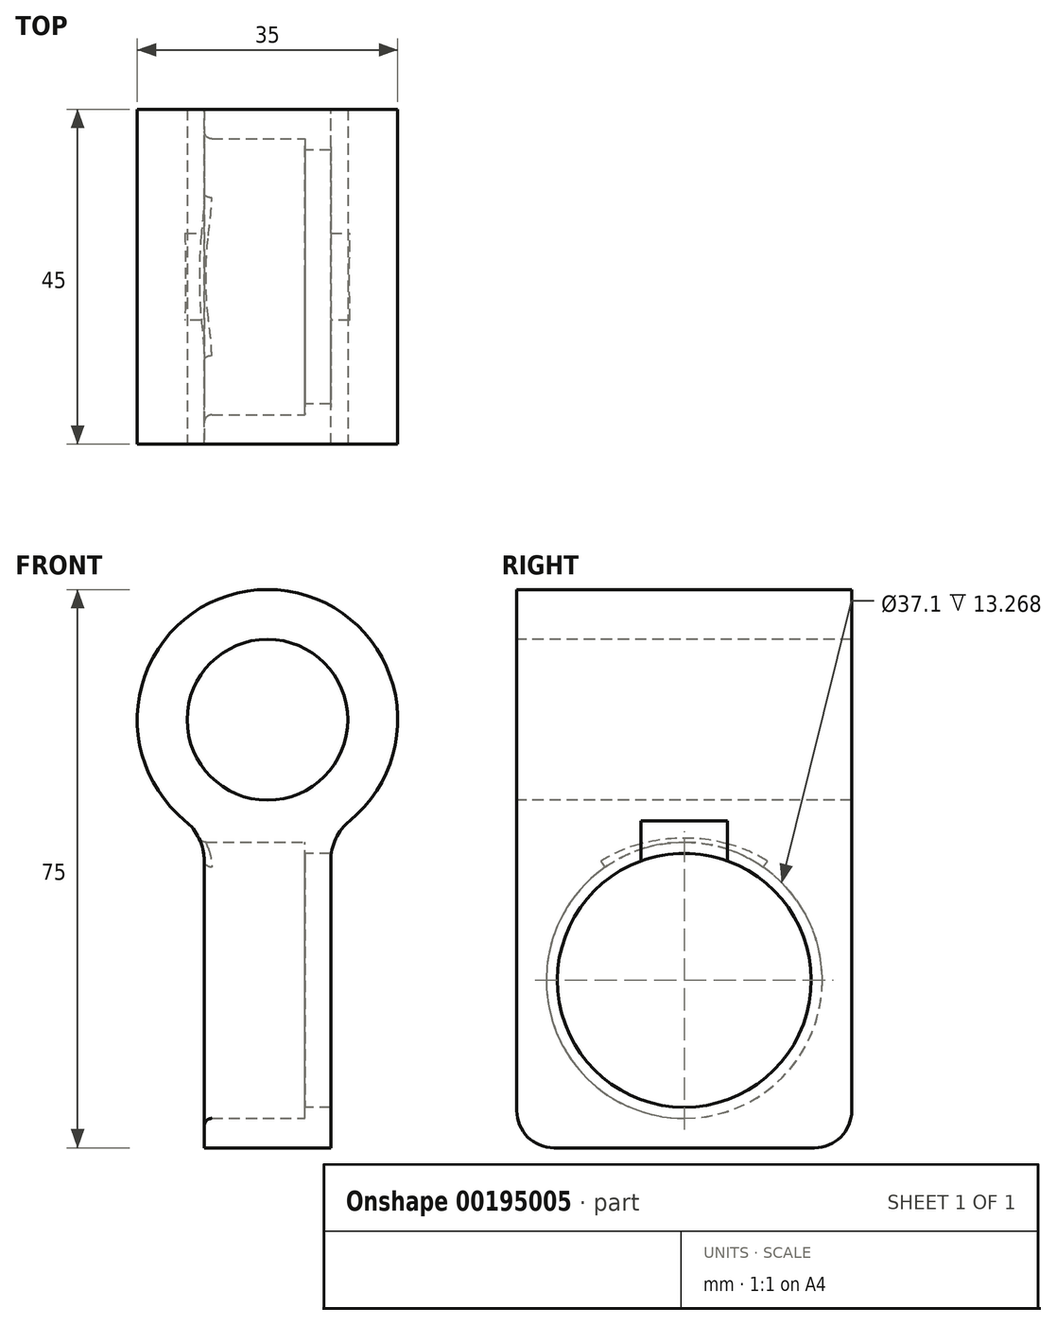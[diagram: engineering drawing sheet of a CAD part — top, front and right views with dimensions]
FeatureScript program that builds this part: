
annotation { "Feature Type Name" : "Feature", "Feature Type Description" : "" }
export const myFeature = defineFeature(function(context is Context, id is Id, definition is map)
    precondition{}
    {
        {
            var Q0;
            Q0=qCreatedBy(makeId("Right.planeOp"),FACE);
            var sketch = newSketch(context, id + "F0", { "sketchPlane" : qUnion([Q0])});
            skCircle(sketch, "E0", {"center": v(0, 0) * mm, "radius": 10.67 * mm});
            skCircle(sketch, "E1", {"center": v(0, 0) * mm, "radius": 7.9 * mm});
            skCircle(sketch, "E2", {"center": v(0, 0) * mm, "radius": 18.55 * mm});
            skCircle(sketch, "E3", {"center": v(0, 0) * mm, "radius": 17.05 * mm});
            skLineSegment(sketch, "E4.bottom", {"start": v(22.5, -22.5) * mm, "end": v(-22.5, -22.5) * mm});
            skLineSegment(sketch, "E4.top", {"start": v(22.5, 22.5) * mm, "end": v(-22.5, 22.5) * mm});
            skLineSegment(sketch, "E4.left", {"start": v(22.5, -22.5) * mm, "end": v(22.5, 22.5) * mm});
            skLineSegment(sketch, "E4.right", {"start": v(-22.5, -22.5) * mm, "end": v(-22.5, 22.5) * mm});
            skSolve(sketch);
        }
        {
            var Q0;
            Q0=qCreatedBy(makeId("Front.planeOp"),FACE);
            var sketch = newSketch(context, id + "F1", { "sketchPlane" : qUnion([Q0])});
            skCircle(sketch, "E5", {"center": v(0, 35) * mm, "radius": 10.8 * mm});
            skCircle(sketch, "E6", {"center": v(0, 35) * mm, "radius": 17.5 * mm});
            skSolve(sketch);
        }
        {
            var Q0;
            Q0=makeQuery(id+"F0.imprint","IMPRINT",FACE,{"disambiguationData":[TD([[makeQuery(id+"F0.imprint","IMPRINT",EDGE,{"derivedFrom":sQuery(id+"F0.wireOp",EDGE,"E2")}),-1.0]])]});
            var Q1;
            Q1=makeQuery(id+"F0.imprint","IMPRINT",FACE,{"disambiguationData":[TD([[makeQuery(id+"F0.imprint","IMPRINT",EDGE,{"derivedFrom":sQuery(id+"F0.wireOp",EDGE,"E2")}),1.0]])]});
            extrude(context, id + "F2", {"entities" : qUnion([Q0, Q1]), "depth" : 17 * mm, "symmetric" : true});
        }
        {
            var Q0;
            Q0=makeQuery(id+"F1.imprint","IMPRINT",FACE,{"disambiguationData":[TD([[makeQuery(id+"F1.imprint","IMPRINT",EDGE,{"derivedFrom":sQuery(id+"F1.wireOp",EDGE,"E5")}),-1.0]])]});
            var Q1;
            Q1=makeQuery(id+"F1.imprint","IMPRINT",FACE,{"disambiguationData":[TD([[makeQuery(id+"F1.imprint","IMPRINT",EDGE,{"derivedFrom":sQuery(id+"F1.wireOp",EDGE,"E5")}),1.0]])]});
            extrude(context, id + "F3", {"entities" : qUnion([Q0, Q1]), "operationType" : NewBodyOperationType.ADD, "depth" : 45 * mm, "symmetric" : true});
        }
        {
            var Q0;
            Q0=makeQuery(id+"F1.imprint","IMPRINT",FACE,{"disambiguationData":[TD([[makeQuery(id+"F1.imprint","IMPRINT",EDGE,{"derivedFrom":sQuery(id+"F1.wireOp",EDGE,"E5")}),1.0]])]});
            extrude(context, id + "F4", {"entities" : qUnion([Q0]), "operationType" : NewBodyOperationType.REMOVE, "oppositeDirection" : true, "depth" : 45 * mm, "symmetric" : true});
        }
        {
            var Q0;
            Q0=makeQuery(id+"F3.boolean.opBoolean","INTERSECT",EDGE,{"derivedFrom":[makeQuery(id+"F2.opExtrude","CAP_FACE",FACE,{"disambiguationData":[OSD([sQuery(id+"F0.wireOp",EDGE,"E3"),sQuery(id+"F0.wireOp",EDGE,"E4.bottom"),sQuery(id+"F0.wireOp",EDGE,"E4.top"),sQuery(id+"F0.wireOp",EDGE,"E4.left"),sQuery(id+"F0.wireOp",EDGE,"E4.right")])],"isStart":true}),makeQuery(id+"F3.opExtrude","SWEPT_FACE",FACE,{"disambiguationData":[OSD([sQuery(id+"F1.wireOp",EDGE,"E6")])]})]});
            var Q1;
            Q1=makeQuery(id+"F3.boolean.opBoolean","INTERSECT",EDGE,{"derivedFrom":[makeQuery(id+"F2.opExtrude","CAP_FACE",FACE,{"disambiguationData":[OSD([sQuery(id+"F0.wireOp",EDGE,"E3"),sQuery(id+"F0.wireOp",EDGE,"E4.bottom"),sQuery(id+"F0.wireOp",EDGE,"E4.top"),sQuery(id+"F0.wireOp",EDGE,"E4.left"),sQuery(id+"F0.wireOp",EDGE,"E4.right")])],"isStart":false}),makeQuery(id+"F3.opExtrude","SWEPT_FACE",FACE,{"disambiguationData":[OSD([sQuery(id+"F1.wireOp",EDGE,"E6")])]})]});
            fillet(context, id + "F5", {"entities" : qUnion([Q0, Q1]), "radius" : 7 * mm, "tangentPropagation" : true, "allowEdgeOverflow" : false});
        }
        {
            var Q0;
            Q0=makeQuery(id+"F0.imprint","IMPRINT",FACE,{"disambiguationData":[TD([[makeQuery(id+"F0.imprint","IMPRINT",EDGE,{"derivedFrom":sQuery(id+"F0.wireOp",EDGE,"E2")}),1.0]])]});
            extrude(context, id + "F6", {"entities" : qUnion([Q0]), "operationType" : NewBodyOperationType.REMOVE, "oppositeDirection" : true, "depth" : 25 * mm, "hasSecondDirection" : true, "secondDirectionOppositeDirection" : false, "secondDirectionDepth" : 5 * mm});
        }
        {
            var Q0;
            Q0=makeQuery(id+"F6.boolean.opBoolean","INTERSECT",EDGE,{"derivedFrom":[makeQuery(id+"F2.opExtrude","CAP_FACE",FACE,{"disambiguationData":[OSD([sQuery(id+"F0.wireOp",EDGE,"E3"),sQuery(id+"F0.wireOp",EDGE,"E4.bottom"),sQuery(id+"F0.wireOp",EDGE,"E4.top"),sQuery(id+"F0.wireOp",EDGE,"E4.left"),sQuery(id+"F0.wireOp",EDGE,"E4.right")])],"isStart":true}),makeQuery(id+"F6.opExtrude","SWEPT_FACE",FACE,{"disambiguationData":[OSD([sQuery(id+"F0.wireOp",EDGE,"E2")])]})]});
            var Q1;
            {var subQ0=sQuery(id+"F1.wireOp",EDGE,"E6");var subQ1=sQuery(id+"F0.wireOp",EDGE,"E4.right");var subQ2=sQuery(id+"F0.wireOp",EDGE,"E4.left");var subQ3=sQuery(id+"F0.wireOp",EDGE,"E4.top");var subQ4=sQuery(id+"F0.wireOp",EDGE,"E4.bottom");var subQ5=sQuery(id+"F0.wireOp",EDGE,"E3");Q1=makeQuery(id+"F6.boolean.opBoolean","INTERSECT",EDGE,{"derivedFrom":[makeQuery(id+"F5.opFillet","BLEND_FACE",FACE,{"disambiguationData":[OSD([subQ5,subQ4,subQ3,subQ2,subQ1,subQ0]),TDD([makeQuery(id+"F3.boolean.opBoolean","INTERSECT",EDGE,{"derivedFrom":[makeQuery(id+"F2.opExtrude","CAP_FACE",FACE,{"disambiguationData":[OSD([subQ5,subQ4,subQ3,subQ2,subQ1])],"isStart":true}),makeQuery(id+"F3.opExtrude","SWEPT_FACE",FACE,{"disambiguationData":[OSD([subQ0])]})]})]),OD(2.0)]}),makeQuery(id+"F6.opExtrude","SWEPT_FACE",FACE,{"disambiguationData":[OSD([sQuery(id+"F0.wireOp",EDGE,"E2")])]})]});}
            var Q2;
            {var subQ0=sQuery(id+"F1.wireOp",EDGE,"E6");var subQ1=sQuery(id+"F0.wireOp",EDGE,"E4.right");var subQ2=sQuery(id+"F0.wireOp",EDGE,"E4.left");var subQ3=sQuery(id+"F0.wireOp",EDGE,"E4.top");var subQ4=sQuery(id+"F0.wireOp",EDGE,"E4.bottom");var subQ5=sQuery(id+"F0.wireOp",EDGE,"E3");Q2=makeQuery(id+"F6.boolean.opBoolean","INTERSECT",EDGE,{"derivedFrom":[makeQuery(id+"F5.opFillet","BLEND_FACE",FACE,{"disambiguationData":[OSD([subQ5,subQ4,subQ3,subQ2,subQ1,subQ0]),TDD([makeQuery(id+"F3.boolean.opBoolean","INTERSECT",EDGE,{"derivedFrom":[makeQuery(id+"F2.opExtrude","CAP_FACE",FACE,{"disambiguationData":[OSD([subQ5,subQ4,subQ3,subQ2,subQ1])],"isStart":true}),makeQuery(id+"F3.opExtrude","SWEPT_FACE",FACE,{"disambiguationData":[OSD([subQ0])]})]})]),OD(1.0)]}),makeQuery(id+"F6.opExtrude","SWEPT_FACE",FACE,{"disambiguationData":[OSD([sQuery(id+"F0.wireOp",EDGE,"E2")])]})]});}
            var Q3;
            {var subQ0=sQuery(id+"F1.wireOp",EDGE,"E6");var subQ1=sQuery(id+"F0.wireOp",EDGE,"E4.right");var subQ2=sQuery(id+"F0.wireOp",EDGE,"E4.left");var subQ3=sQuery(id+"F0.wireOp",EDGE,"E4.top");var subQ4=sQuery(id+"F0.wireOp",EDGE,"E4.bottom");var subQ5=sQuery(id+"F0.wireOp",EDGE,"E3");Q3=makeQuery(id+"F6.boolean.opBoolean","INTERSECT",EDGE,{"derivedFrom":[makeQuery(id+"F5.opFillet","BLEND_FACE",FACE,{"disambiguationData":[OSD([subQ5,subQ4,subQ3,subQ2,subQ1,subQ0]),TDD([makeQuery(id+"F3.boolean.opBoolean","INTERSECT",EDGE,{"derivedFrom":[makeQuery(id+"F2.opExtrude","CAP_FACE",FACE,{"disambiguationData":[OSD([subQ5,subQ4,subQ3,subQ2,subQ1])],"isStart":true}),makeQuery(id+"F3.opExtrude","SWEPT_FACE",FACE,{"disambiguationData":[OSD([subQ0])]})]})]),OD(0.0)]}),makeQuery(id+"F6.opExtrude","SWEPT_FACE",FACE,{"disambiguationData":[OSD([sQuery(id+"F0.wireOp",EDGE,"E2")])]})]});}
            fillet(context, id + "F7", {"entities" : qUnion([Q0, Q1, Q2, Q3]), "radius" : 1 * mm, "tangentPropagation" : true, "allowEdgeOverflow" : false});
        }
        {
            var Q0;
            Q0=makeQuery(id+"F2.opExtrude","SWEPT_EDGE",EDGE,{"disambiguationData":[OSD([sQuery(id+"F0.wireOp",EDGE,"E4.bottom"),sQuery(id+"F0.wireOp",EDGE,"E4.left")])]});
            var Q1;
            Q1=makeQuery(id+"F2.opExtrude","SWEPT_EDGE",EDGE,{"disambiguationData":[OSD([sQuery(id+"F0.wireOp",EDGE,"E4.bottom"),sQuery(id+"F0.wireOp",EDGE,"E4.right")])]});
            fillet(context, id + "F8", {"entities" : qUnion([Q0, Q1]), "radius" : 5 * mm, "tangentPropagation" : true, "allowEdgeOverflow" : false});
        }
    });
